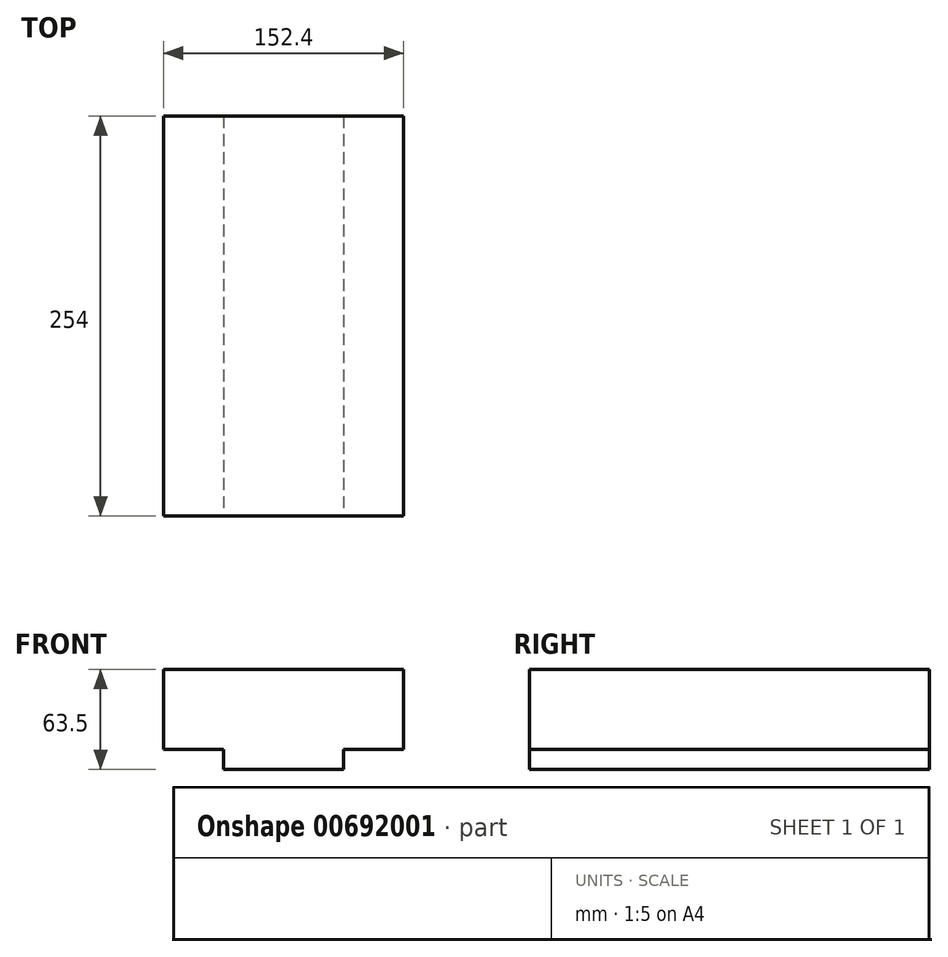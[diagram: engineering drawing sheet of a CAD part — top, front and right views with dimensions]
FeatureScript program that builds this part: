
annotation { "Feature Type Name" : "Feature", "Feature Type Description" : "" }
export const myFeature = defineFeature(function(context is Context, id is Id, definition is map)
    precondition{}
    {
        {
            var Q0;
            Q0=qCreatedBy(makeId("Front.planeOp"),FACE);
            var sketch = newSketch(context, id + "F0", { "sketchPlane" : qUnion([Q0])});
            skLineSegment(sketch, "E0.bottom", {"start": v(76.2, 38.1) * mm, "end": v(-76.2, 38.1) * mm});
            skLineSegment(sketch, "E0.top", {"start": v(76.2, -38.1) * mm, "end": v(-76.2, -38.1) * mm});
            skLineSegment(sketch, "E0.left", {"start": v(76.2, 38.1) * mm, "end": v(76.2, -38.1) * mm});
            skLineSegment(sketch, "E0.right", {"start": v(-76.2, 38.1) * mm, "end": v(-76.2, -38.1) * mm});
            skPoint(sketch, "E0.middle", {"position": v(0, 0) * mm});
            skLineSegment(sketch, "E1.bottom", {"start": v(38.1, -50.8) * mm, "end": v(-38.1, -50.8) * mm});
            skLineSegment(sketch, "E1.top", {"start": v(38.1, -25.4) * mm, "end": v(-38.1, -25.4) * mm});
            skLineSegment(sketch, "E1.left", {"start": v(38.1, -50.8) * mm, "end": v(38.1, -25.4) * mm});
            skLineSegment(sketch, "E1.right", {"start": v(-38.1, -50.8) * mm, "end": v(-38.1, -25.4) * mm});
            skPoint(sketch, "E1.middle", {"position": v(0, -38.1) * mm});
            skSolve(sketch);
        }
        {
            var Q0;
            Q0=makeQuery(id+"F0.imprint","IMPRINT",FACE,{"disambiguationData":[TD([[makeQuery(id+"F0.imprint","IMPRINT",EDGE,{"derivedFrom":sQuery(id+"F0.wireOp",EDGE,"E0.bottom")}),1.0]])]});
            var Q1;
            {var subQ5=sQuery(id+"F0.wireOp",EDGE,"E1.top");Q1=makeQuery(id+"F0.imprint","IMPRINT",FACE,{"disambiguationData":[TD([[makeQuery(id+"F0.imprint","IMPRINT",EDGE,{"derivedFrom":subQ5}),1.0]])]});}
            var Q2;
            {var subQ5=sQuery(id+"F0.wireOp",EDGE,"E1.bottom");Q2=makeQuery(id+"F0.imprint","IMPRINT",FACE,{"disambiguationData":[TD([[makeQuery(id+"F0.imprint","IMPRINT",EDGE,{"derivedFrom":subQ5}),-1.0]])]});}
            extrude(context, id + "F1", {"entities" : qUnion([Q0, Q1, Q2]), "oppositeDirection" : true, "depth" : 254 * mm, "offsetDistance" : 25.4 * mm});
        }
        {
            var Q0;
            Q0=makeQuery(id+"F1.opExtrude","SWEPT_FACE",FACE,{"disambiguationData":[OSD([sQuery(id+"F0.wireOp",EDGE,"E0.right")])]});
            var sketch = newSketch(context, id + "F2", { "sketchPlane" : qUnion([Q0])});
            skLineSegment(sketch, "E2", {"start": v(0, -38.1) * mm, "end": v(0, -31.75) * mm});
            skLineSegment(sketch, "E3", {"start": v(0, -31.75) * mm, "end": v(-254, -31.75) * mm});
            skLineSegment(sketch, "E4", {"start": v(0, -31.75) * mm, "end": v(0, 6.35) * mm});
            skLineSegment(sketch, "E5", {"start": v(0, 6.35) * mm, "end": v(-254, 6.35) * mm});
            skLineSegment(sketch, "E6", {"start": v(0, 6.35) * mm, "end": v(-101.6, 6.35) * mm});
            skLineSegment(sketch, "E7", {"start": v(-101.6, 6.35) * mm, "end": v(-254, -31.75) * mm});
            skLineSegment(sketch, "E8", {"start": v(-101.6, 6.35) * mm, "end": v(-50.8, 6.35) * mm});
            skLineSegment(sketch, "E9", {"start": v(-50.8, 6.35) * mm, "end": v(-50.8, -6.35) * mm});
            skLineSegment(sketch, "E10", {"start": v(-50.8, -6.35) * mm, "end": v(-101.6, 6.35) * mm});
            skLineSegment(sketch, "E11", {"start": v(0, -31.75) * mm, "end": v(0, -28.57) * mm});
            skLineSegment(sketch, "E12", {"start": v(0, -31.75) * mm, "end": v(-6.35, -31.75) * mm});
            skLineSegment(sketch, "E13", {"start": v(-6.35, -31.75) * mm, "end": v(0, -28.57) * mm});
            skLineSegment(sketch, "E14", {"start": v(0, -28.57) * mm, "end": v(-50.8, -6.35) * mm});
            skLineSegment(sketch, "E15", {"start": v(0, 6.35) * mm, "end": v(0, 12.7) * mm});
            skLineSegment(sketch, "E16", {"start": v(0, 12.7) * mm, "end": v(-254, 12.7) * mm});
            skSolve(sketch);
        }
        {
            var Q0;
            {var subQ0=sQuery(id+"F2.wireOp",EDGE,"E16");Q0=makeQuery(id+"F2.imprint","IMPRINT",FACE,{"disambiguationData":[TD([[makeQuery(id+"F2.imprint","IMPRINT",EDGE,{"derivedFrom":subQ0}),-1.0]])]});}
            extrude(context, id + "F3", {"entities" : qUnion([Q0]), "operationType" : NewBodyOperationType.REMOVE, "endBound" : BoundingType.THROUGH_ALL, "oppositeDirection" : true, "depth" : 25.4 * mm, "offsetDistance" : 25.4 * mm});
        }
    });
